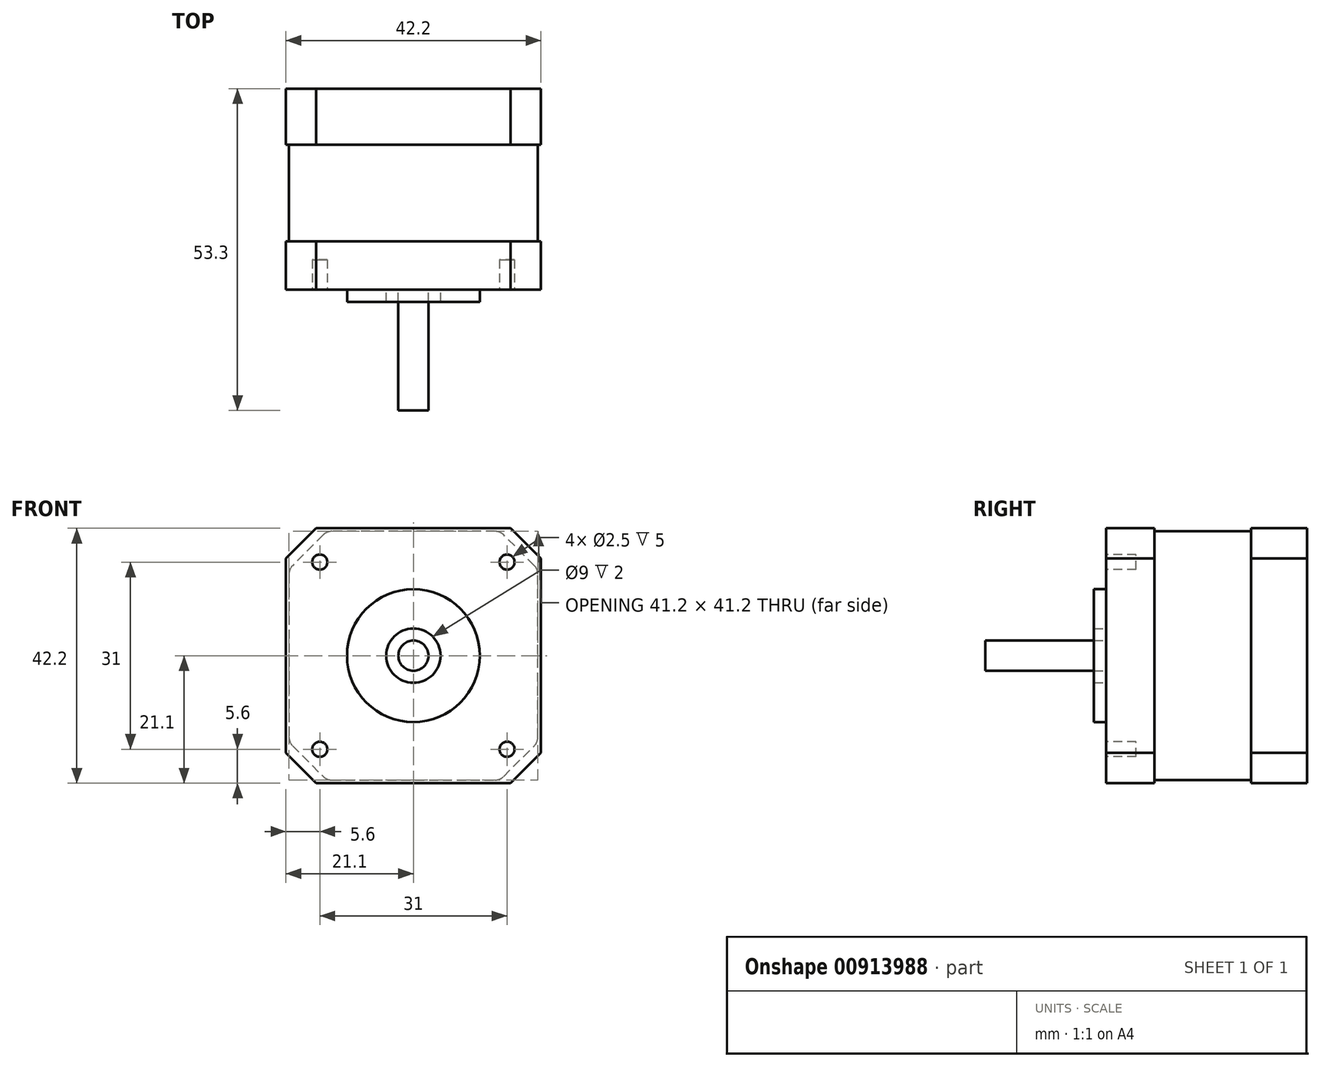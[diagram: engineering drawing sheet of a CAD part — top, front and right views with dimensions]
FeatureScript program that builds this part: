
annotation { "Feature Type Name" : "Feature", "Feature Type Description" : "" }
export const myFeature = defineFeature(function(context is Context, id is Id, definition is map)
    precondition{}
    {
        {
            var Q0;
            Q0=qCreatedBy(makeId("Front.planeOp"),FACE);
            var sketch = newSketch(context, id + "F0", { "sketchPlane" : qUnion([Q0])});
            skLineSegment(sketch, "E0.bottom", {"start": v(-21.1, 21.1) * mm, "end": v(21.1, 21.1) * mm});
            skLineSegment(sketch, "E0.top", {"start": v(-21.1, -21.1) * mm, "end": v(21.1, -21.1) * mm});
            skLineSegment(sketch, "E0.left", {"start": v(-21.1, 21.1) * mm, "end": v(-21.1, -21.1) * mm});
            skLineSegment(sketch, "E0.right", {"start": v(21.1, 21.1) * mm, "end": v(21.1, -21.1) * mm});
            skLineSegment(sketch, "E1", {"start": v(-21.1, 21.1) * mm, "end": v(21.1, -21.1) * mm, "construction": true});
            skCircle(sketch, "E2", {"center": v(0, 0) * mm, "radius": 2.5 * mm});
            skSolve(sketch);
        }
        {
            var Q0;
            Q0=makeQuery(id+"F0.imprint","IMPRINT",FACE,{"disambiguationData":[TD([[makeQuery(id+"F0.imprint","IMPRINT",EDGE,{"derivedFrom":sQuery(id+"F0.wireOp",EDGE,"E2")}),1.0]])]});
            var Q1;
            Q1=makeQuery(id+"F0.imprint","IMPRINT",FACE,{"disambiguationData":[TD([[makeQuery(id+"F0.imprint","IMPRINT",EDGE,{"derivedFrom":sQuery(id+"F0.wireOp",EDGE,"E0.bottom")}),-1.0]])]});
            extrude(context, id + "F1", {"entities" : qUnion([Q0, Q1]), "oppositeDirection" : true, "depth" : 33.3 * mm, "offsetDistance" : 25 * mm});
        }
        {
            var Q0;
            Q0=makeQuery(id+"F1.opExtrude","SWEPT_EDGE",EDGE,{"disambiguationData":[OSD([sQuery(id+"F0.wireOp",EDGE,"E0.bottom"),sQuery(id+"F0.wireOp",EDGE,"E0.right")])]});
            var Q1;
            Q1=makeQuery(id+"F1.opExtrude","SWEPT_EDGE",EDGE,{"disambiguationData":[OSD([sQuery(id+"F0.wireOp",EDGE,"E0.bottom"),sQuery(id+"F0.wireOp",EDGE,"E0.left")])]});
            var Q2;
            Q2=makeQuery(id+"F1.opExtrude","SWEPT_EDGE",EDGE,{"disambiguationData":[OSD([sQuery(id+"F0.wireOp",EDGE,"E0.top"),sQuery(id+"F0.wireOp",EDGE,"E0.right")])]});
            var Q3;
            Q3=makeQuery(id+"F1.opExtrude","SWEPT_EDGE",EDGE,{"disambiguationData":[OSD([sQuery(id+"F0.wireOp",EDGE,"E0.top"),sQuery(id+"F0.wireOp",EDGE,"E0.left")])]});
            chamfer(context, id + "F2", {"entities" : qUnion([Q0, Q1, Q2, Q3]), "width" : 5 * mm, "tangentPropagation" : true});
        }
        {
            var Q0;
            Q0=makeQuery(id+"F0.imprint","IMPRINT",FACE,{"disambiguationData":[TD([[makeQuery(id+"F0.imprint","IMPRINT",EDGE,{"derivedFrom":sQuery(id+"F0.wireOp",EDGE,"E2")}),1.0]])]});
            extrude(context, id + "F3", {"entities" : qUnion([Q0]), "operationType" : NewBodyOperationType.ADD, "depth" : 20 * mm, "offsetDistance" : 25 * mm});
        }
        {
            var Q0;
            Q0=makeQuery(id+"F1.opExtrude","CAP_FACE",FACE,{"disambiguationData":[OSD([sQuery(id+"F0.wireOp",EDGE,"E0.bottom"),sQuery(id+"F0.wireOp",EDGE,"E0.top"),sQuery(id+"F0.wireOp",EDGE,"E0.left"),sQuery(id+"F0.wireOp",EDGE,"E0.right")])],"isStart":true});
            var sketch = newSketch(context, id + "F4", { "sketchPlane" : qUnion([Q0])});
            skCircle(sketch, "E3", {"center": v(0, 0) * mm, "radius": 4.5 * mm});
            skCircle(sketch, "E4", {"center": v(0, 0) * mm, "radius": 11 * mm});
            skSolve(sketch);
        }
        {
            var Q0;
            Q0=qSketchRegion(id+"F4",true);
            extrude(context, id + "F5", {"entities" : qUnion([Q0]), "operationType" : NewBodyOperationType.ADD, "depth" : 2 * mm, "offsetDistance" : 25 * mm});
        }
        {
            var Q0;
            {var subQ0=sQuery(id+"F0.wireOp",EDGE,"E0.left");var subQ1=sQuery(id+"F0.wireOp",EDGE,"E0.bottom");var subQ2=sQuery(id+"F0.wireOp",EDGE,"E0.top");var subQ3=sQuery(id+"F0.wireOp",EDGE,"E0.right");Q0=makeQuery(id+"F5.boolean.opBoolean","SPLIT",FACE,{"disambiguationData":[TD([makeQuery(id+"F1.opExtrude","SWEPT_FACE",FACE,{"disambiguationData":[OSD([subQ1])]})])],"derivedFrom":makeQuery(id+"F1.opExtrude","CAP_FACE",FACE,{"disambiguationData":[OSD([subQ1,subQ2,subQ0,subQ3])],"isStart":true})});}
            var sketch = newSketch(context, id + "F6", { "sketchPlane" : qUnion([Q0])});
            skCircle(sketch, "E5", {"center": v(-15.5, 15.5) * mm, "radius": 1.25 * mm});
            skCircle(sketch, "E6.1.0", {"center": v(-15.5, -15.5) * mm, "radius": 1.25 * mm});
            skCircle(sketch, "E6.2.0", {"center": v(15.5, -15.5) * mm, "radius": 1.25 * mm});
            skCircle(sketch, "E6.3.0", {"center": v(15.5, 15.5) * mm, "radius": 1.25 * mm});
            skPoint(sketch, "E6.center", {"position": v(0, 0) * mm});
            skSolve(sketch);
        }
        {
            var Q0;
            Q0=qSketchRegion(id+"F6",true);
            extrude(context, id + "F7", {"entities" : qUnion([Q0]), "operationType" : NewBodyOperationType.REMOVE, "oppositeDirection" : true, "depth" : 5 * mm, "offsetDistance" : 25 * mm});
        }
        {
            var Q0;
            {var subQ0=sQuery(id+"F0.wireOp",EDGE,"E0.left");var subQ1=sQuery(id+"F0.wireOp",EDGE,"E0.bottom");var subQ2=sQuery(id+"F0.wireOp",EDGE,"E0.top");var subQ3=sQuery(id+"F0.wireOp",EDGE,"E0.right");Q0=makeQuery(id+"F5.boolean.opBoolean","SPLIT",FACE,{"disambiguationData":[TD([makeQuery(id+"F1.opExtrude","SWEPT_FACE",FACE,{"disambiguationData":[OSD([subQ1])]})])],"derivedFrom":makeQuery(id+"F1.opExtrude","CAP_FACE",FACE,{"disambiguationData":[OSD([subQ1,subQ2,subQ0,subQ3])],"isStart":true})});}
            cPlane(context, id + "F8", {"entities" : qUnion([Q0]), "cplaneType" : CPlaneType.OFFSET, "offset" : 8 * mm, "oppositeDirection" : true, "width" : 150 * mm, "height" : 150 * mm});
        }
        {
            var Q0;
            Q0=qCreatedBy(id+"F8.planeOp",FACE);
            var sketch = newSketch(context, id + "F9", { "sketchPlane" : qUnion([Q0])});
            skLineSegment(sketch, "E7", {"start": v(0, 0) * mm, "end": v(0, 20.6) * mm});
            skLineSegment(sketch, "E8", {"start": v(0, 20.6) * mm, "end": v(-14.34, 20.6) * mm});
            skLineSegment(sketch, "E9", {"start": v(-14.34, 20.6) * mm, "end": v(-20.6, 14.34) * mm});
            skLineSegment(sketch, "E10", {"start": v(-20.6, 14.34) * mm, "end": v(-20.6, 0) * mm});
            skLineSegment(sketch, "E11", {"start": v(-20.6, 0) * mm, "end": v(0, 0) * mm});
            skLineSegment(sketch, "E12.1.0", {"start": v(-20.6, 0) * mm, "end": v(-20.6, -14.34) * mm});
            skLineSegment(sketch, "E12.1.1", {"start": v(-14.34, -20.6) * mm, "end": v(0, -20.6) * mm});
            skLineSegment(sketch, "E12.1.2", {"start": v(-20.6, -14.34) * mm, "end": v(-14.34, -20.6) * mm});
            skLineSegment(sketch, "E12.2.0", {"start": v(0, -20.6) * mm, "end": v(14.34, -20.6) * mm});
            skLineSegment(sketch, "E12.2.1", {"start": v(20.6, -14.34) * mm, "end": v(20.6, 0) * mm});
            skLineSegment(sketch, "E12.2.2", {"start": v(14.34, -20.6) * mm, "end": v(20.6, -14.34) * mm});
            skLineSegment(sketch, "E12.3.0", {"start": v(20.6, 0) * mm, "end": v(20.6, 14.34) * mm});
            skLineSegment(sketch, "E12.3.1", {"start": v(14.34, 20.6) * mm, "end": v(0, 20.6) * mm});
            skLineSegment(sketch, "E12.3.2", {"start": v(20.6, 14.34) * mm, "end": v(14.34, 20.6) * mm});
            skPoint(sketch, "E12.center", {"position": v(0, 0) * mm});
            skLineSegment(sketch, "E13.bottom", {"start": v(-24.85, 25.17) * mm, "end": v(25.9, 25.17) * mm});
            skLineSegment(sketch, "E13.top", {"start": v(-24.85, -25.03) * mm, "end": v(25.9, -25.03) * mm});
            skLineSegment(sketch, "E13.left", {"start": v(-24.85, 25.17) * mm, "end": v(-24.85, -25.03) * mm});
            skLineSegment(sketch, "E13.right", {"start": v(25.9, 25.17) * mm, "end": v(25.9, -25.03) * mm});
            skSolve(sketch);
        }
        {
            var Q0;
            Q0=qSketchRegion(id+"F9",true);
            extrude(context, id + "F10", {"entities" : qUnion([Q0]), "operationType" : NewBodyOperationType.REMOVE, "oppositeDirection" : true, "depth" : 16 * mm, "offsetDistance" : 25 * mm});
        }
        {
            var Q0;
            Q0=makeQuery(id+"F10.boolean.opBoolean","COPY",EDGE,{"derivedFrom":makeQuery(id+"F10.opExtrude","SWEPT_EDGE",EDGE,{"disambiguationData":[OSD([sQuery(id+"F9.wireOp",EDGE,"E12.3.0"),sQuery(id+"F9.wireOp",EDGE,"E12.3.2")])]})});
            var Q1;
            Q1=makeQuery(id+"F10.boolean.opBoolean","COPY",EDGE,{"derivedFrom":makeQuery(id+"F10.opExtrude","SWEPT_EDGE",EDGE,{"disambiguationData":[OSD([sQuery(id+"F9.wireOp",EDGE,"E12.3.1"),sQuery(id+"F9.wireOp",EDGE,"E12.3.2")])]})});
            var Q2;
            Q2=makeQuery(id+"F10.boolean.opBoolean","COPY",EDGE,{"derivedFrom":makeQuery(id+"F10.opExtrude","SWEPT_EDGE",EDGE,{"disambiguationData":[OSD([sQuery(id+"F9.wireOp",EDGE,"E8"),sQuery(id+"F9.wireOp",EDGE,"E9")])]})});
            var Q3;
            Q3=makeQuery(id+"F10.boolean.opBoolean","COPY",EDGE,{"derivedFrom":makeQuery(id+"F10.opExtrude","SWEPT_EDGE",EDGE,{"disambiguationData":[OSD([sQuery(id+"F9.wireOp",EDGE,"E9"),sQuery(id+"F9.wireOp",EDGE,"E10")])]})});
            var Q4;
            Q4=makeQuery(id+"F10.boolean.opBoolean","COPY",EDGE,{"derivedFrom":makeQuery(id+"F10.opExtrude","SWEPT_EDGE",EDGE,{"disambiguationData":[OSD([sQuery(id+"F9.wireOp",EDGE,"E12.1.0"),sQuery(id+"F9.wireOp",EDGE,"E12.1.2")])]})});
            var Q5;
            Q5=makeQuery(id+"F10.boolean.opBoolean","COPY",EDGE,{"derivedFrom":makeQuery(id+"F10.opExtrude","SWEPT_EDGE",EDGE,{"disambiguationData":[OSD([sQuery(id+"F9.wireOp",EDGE,"E12.1.1"),sQuery(id+"F9.wireOp",EDGE,"E12.1.2")])]})});
            var Q6;
            Q6=makeQuery(id+"F10.boolean.opBoolean","COPY",EDGE,{"derivedFrom":makeQuery(id+"F10.opExtrude","SWEPT_EDGE",EDGE,{"disambiguationData":[OSD([sQuery(id+"F9.wireOp",EDGE,"E12.2.1"),sQuery(id+"F9.wireOp",EDGE,"E12.2.2")])]})});
            var Q7;
            Q7=makeQuery(id+"F10.boolean.opBoolean","COPY",EDGE,{"derivedFrom":makeQuery(id+"F10.opExtrude","SWEPT_EDGE",EDGE,{"disambiguationData":[OSD([sQuery(id+"F9.wireOp",EDGE,"E12.2.0"),sQuery(id+"F9.wireOp",EDGE,"E12.2.2")])]})});
            fillet(context, id + "F11", {"entities" : qUnion([Q0, Q1, Q2, Q3, Q4, Q5, Q6, Q7]), "radius" : 2 * mm, "tangentPropagation" : true, "allowEdgeOverflow" : false});
        }
    });
